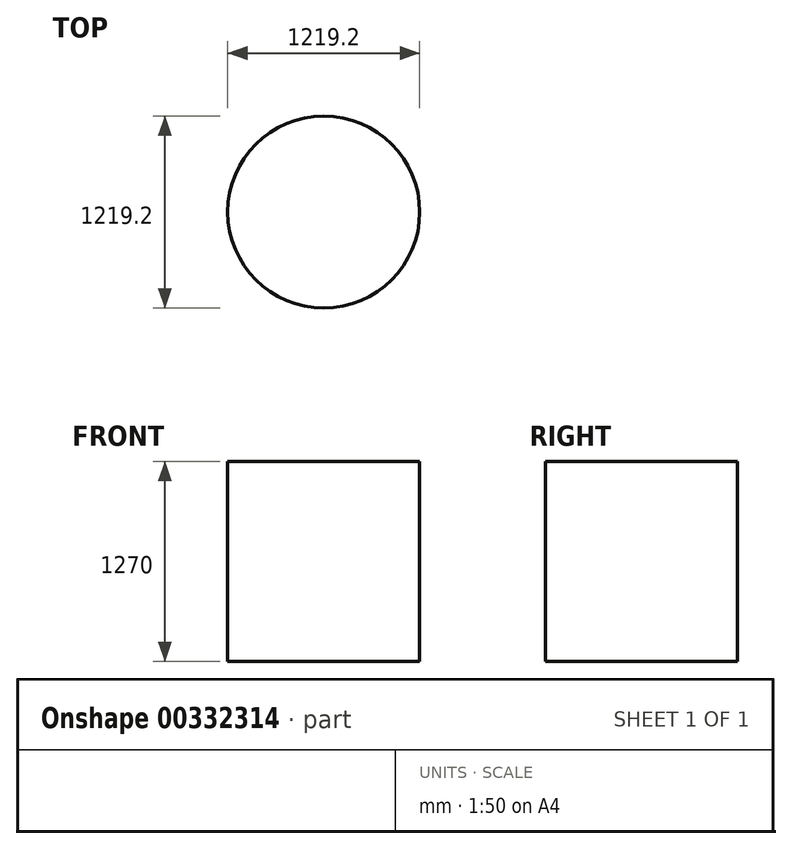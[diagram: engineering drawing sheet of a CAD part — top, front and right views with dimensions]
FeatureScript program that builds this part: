
annotation { "Feature Type Name" : "Feature", "Feature Type Description" : "" }
export const myFeature = defineFeature(function(context is Context, id is Id, definition is map)
    precondition{}
    {
        {
            var Q0;
            Q0=qCreatedBy(makeId("Top.planeOp"),FACE);
            var sketch = newSketch(context, id + "F0", { "sketchPlane" : qUnion([Q0])});
            skCircle(sketch, "E0", {"center": v(0, 0) * mm, "radius": 609.6 * mm});
            skSolve(sketch);
        }
        {
            var Q0;
            Q0=makeQuery(id+"F0.imprint","IMPRINT",FACE,{"disambiguationData":[TD([[makeQuery(id+"F0.imprint","IMPRINT",EDGE,{"derivedFrom":sQuery(id+"F0.wireOp",EDGE,"E0")}),1.0]])]});
            extrude(context, id + "F1", {"entities" : qUnion([Q0]), "depth" : 1270 * mm});
        }
    });
